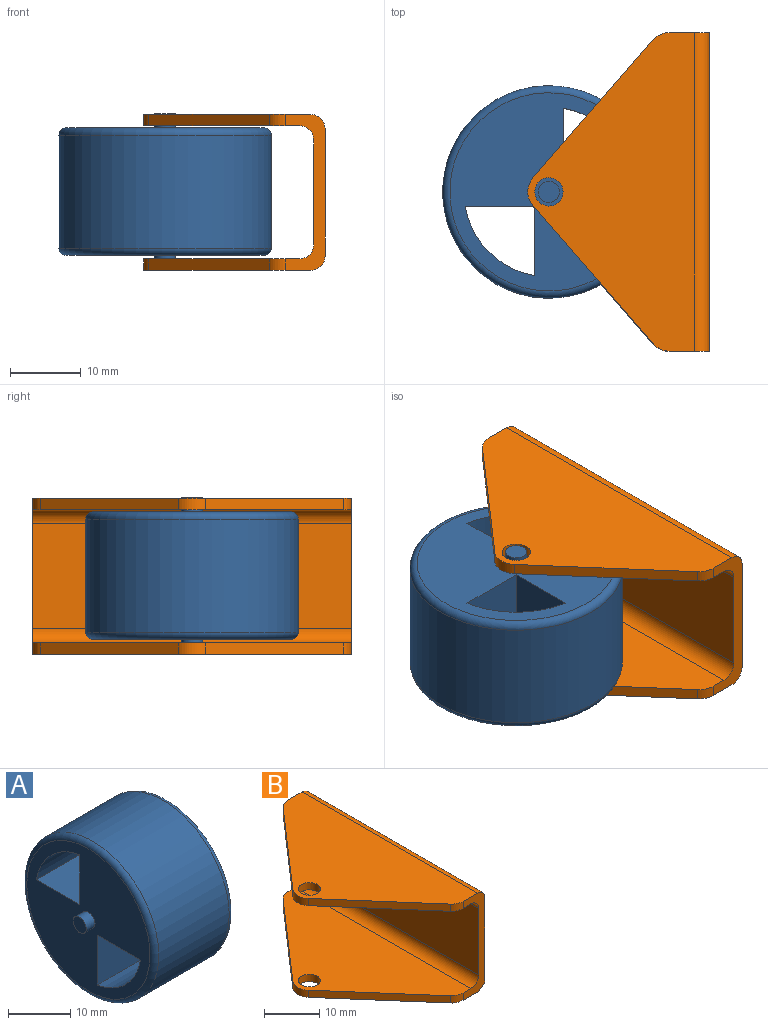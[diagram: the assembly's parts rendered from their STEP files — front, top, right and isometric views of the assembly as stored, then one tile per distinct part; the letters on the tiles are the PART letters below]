
ASSEMBLY  parts=2 mates=1
PART A: 15 faces, bbox 22x32.5x32.5 mm
  f0: cylinder r=12mm len=18mm, axis (-1,0,0), area 267mm2, adj f1,f6,f7,f8
  f1: plane 18x9.83mm, normal (0,0,1), area 177mm2, adj f0,f6,f7,f8
  f2: cylinder r=12mm len=18mm, axis (-1,0,0), area 267mm2, adj f3,f5,f7,f8
  f3: plane 18x9.83mm, normal (0,0,-1), area 177mm2, adj f2,f5,f7,f8
  f4: cylinder r=15mm len=30mm, axis (-1,0,0), area 1508mm2, adj f9,f10
  f5: plane 18x9.83mm, normal (0,-1,0), area 177mm2, adj f2,f3,f7,f8
  f6: plane 18x9.83mm, normal (0,1,0), area 177mm2, adj f0,f1,f7,f8
  f7: plane 28x28mm, normal (1,0,0), area 470mm2, adj f0,f1,f2,f3,f5,f6,f10,f11
  f8: plane 28x28mm, normal (-1,0,0), area 470mm2, adj f0,f1,f2,f3,f5,f6,f9,f13
  f9: torus R=14mm, axis (1,0,0), area 144.5mm2, adj f4,f8
  f10: torus R=14mm, axis (1,0,0), area 144.5mm2, adj f4,f7
  f11: cylinder r=1.5mm len=3mm, axis (-1,0,0), area 18.8mm2, adj f7,f12
  f12: plane 3x3mm, normal (1,0,0), area 7.1mm2, adj f11
  f13: cylinder r=1.5mm len=3mm, axis (1,0,0), area 18.8mm2, adj f8,f14
  f14: plane 3x3mm, normal (-1,0,0), area 7.1mm2, adj f13
PART B: 24 faces, bbox 25.6x45x22 mm
  f0: plane 45x23.62mm, normal (0,0,1), area 651.5mm2, adj f1,f3,f14,f15,f16,f17,f18,f19
  f1: plane 22x5.63mm, normal (0,-1,0), area 48.1mm2, adj f0,f2,f4,f5,f6,f7,f12,f14
  f2: plane 45x23.62mm, normal (0,0,-1), area 651.5mm2, adj f1,f3,f8,f9,f10,f11,f12,f13
  f3: plane 22x5.63mm, normal (0,1,0), area 48.1mm2, adj f0,f2,f4,f5,f6,f7,f8,f18
  f4: plane 45x22.02mm, normal (0,0,-1), area 579.5mm2, adj f1,f3,f14,f15,f16,f17,f18,f19
  f5: plane 45x22.02mm, normal (0,0,1), area 579.5mm2, adj f1,f3,f8,f9,f10,f11,f12,f13
  f6: plane 45x14.8mm, normal (-1,0,0), area 666mm2, adj f1,f3,f20,f21
  f7: plane 45x18mm, normal (1,0,0), area 810mm2, adj f1,f3,f22,f23
  f8: cylinder r=3mm len=2.26mm, axis (0,0,1), area 4.1mm2, adj f2,f3,f5,f9
  f9: plane 19.5x16.99mm, normal (-0.75,0.66,0), area 41.4mm2, adj f2,f5,f8,f10
  f10: cylinder r=3mm len=3.94mm, axis (0,0,1), area 6.9mm2, adj f2,f5,f9,f11
  f11: plane 19.5x16.99mm, normal (-0.75,-0.66,0), area 41.4mm2, adj f2,f5,f10,f12
  f12: cylinder r=3mm len=2.26mm, axis (0,0,1), area 4.1mm2, adj f1,f2,f5,f11
  f13: cylinder r=2mm len=4mm, axis (0,0,1), area 20.1mm2, adj f2,f5
  f14: cylinder r=3mm len=2.26mm, axis (0,0,1), area 4.1mm2, adj f0,f1,f4,f15
  f15: plane 19.5x16.99mm, normal (-0.75,-0.66,0), area 41.4mm2, adj f0,f4,f14,f16
  f16: cylinder r=3mm len=3.94mm, axis (0,0,1), area 6.9mm2, adj f0,f4,f15,f17
  f17: plane 19.5x16.99mm, normal (-0.75,0.66,0), area 41.4mm2, adj f0,f4,f16,f18
  f18: cylinder r=3mm len=2.26mm, axis (0,0,1), area 4.1mm2, adj f0,f3,f4,f17
  f19: cylinder r=2mm len=4mm, axis (0,0,1), area 20.1mm2, adj f0,f4
  f20: cylinder r=2mm len=45mm, axis (0,-1,0), area 141.4mm2, adj f1,f3,f5,f6
  f21: cylinder r=2mm len=45mm, axis (0,1,0), area 141.4mm2, adj f1,f3,f4,f6
  f22: cylinder r=2mm len=45mm, axis (0,-1,0), area 141.4mm2, adj f1,f2,f3,f7
  f23: cylinder r=2mm len=45mm, axis (0,1,0), area 141.4mm2, adj f0,f1,f3,f7
PLACE A rot(axis=(0.71,0,-0.71),180deg) t=(-21.02,3.9,8.47)mm
PLACE B at identity
MATE cylindrical A.f11 <-> B.f10  axis (0,0,1) through (-21.02,3.9,-10.53)mm
